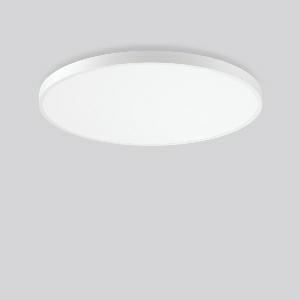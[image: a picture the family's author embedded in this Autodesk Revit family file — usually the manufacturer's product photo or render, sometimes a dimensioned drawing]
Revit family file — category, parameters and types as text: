
# Revit family: triona_round_a_312391_002_2_76_6565
name_source: partatom
category: Lighting Fixtures
units: mm (PartAtom-declared; Revit-internal decimal feet)

## family parameters
Cut with Voids When Loaded = No
Host = Face
Light Source = No
Part Type = Normal
Room Calculation Point = No
Round Connector Dimension = Use Diameter
Shared = No

## types (1)
- TuneableWhite 846 (1 x LED Modul 846, 5700 lm, 4600)
    Apparent Load = 61 VA
    CIE Flux Codes = 50 80 96 100 100
    Color Rendering = 80
    Color Temperature = 4600
    Default Elevation = 1800 mm
    Description = Series: TRIONA round
Decorative round LED surface-mounted luminaire. Flat, seamless frame: aluminium extrusion profile, powder coated. Cover made of sheet steel, powder-coated. Light emission through a diffuser: plastic, opal. Lightguide and diffuser made of non-yellowing plastic (PMMA). Lateral light emission (RZB SIDELITE technology) for above-average homogeneous light distribution. Tunable white versions, dynamically adjustable from 2700 K to 6500 K. Suitable for Ceiling mounting, Wall (surface). Tool-free mounting via bayonet connection. Electronic ballast included. Very easy installation thanks to Plug+Play connection. Ideal for use as part of the Human Centric Lighting concept in connection with RZB light management systems. 
Colour: traffic white, matt (RAL 9016)
Diameter: 1009 mm
Height: 88 mm
Lamp: LED
Socket: without socket
Colour temperature: 2700K - 6500K
Colour rendering index (CRI): 80
System power: 61 W
Rated luminous flux: 5700 lm
Luminous efficiency: 93 lm/W
System power 2: 63 W
Rated luminous flux 2: 5450 lm
Luminous efficiency 2: 87 lm/W
System power 3: 63 W
Rated luminous flux 3: 5500 lm
Luminous efficiency 3: 87 lm/W
Control gear: Converter, dimmable, DALI
Protection class: I
Type of protection: IP 20
    Height = 88 mm
    Lamp = 1 x LED Modul 846
    Lamp Light Flux = 5700 lm
    Lamp count = 1
    Length = 1009 mm
    Lifetime = 50000 h
    Luminous efficacy = 93 lm/W
    Manufacturer = RZB
    ModVariant = No
    Model = 312391.002.2.76
    Mounting Place = Ceiling
    Mounting Type = Surface mounted
    Number of Poles = 1
    OnlyDefault = Yes
    Power Factor = 1
    Product Name = TRIONA round A
    Product group = Surface mounted modular luminaires
    ProductGroupID = 306
    Protection Class = Protection class I
    Protection Degree = IP 20
    RLX_Detail_Level = 1
    RLX_Emergency_Light_Flux = 0 lm
    RLX_Emergency_Type = 0
    RLX_Emergency_Type_DB = No
    RlxData = <blob elided: 36333 chars, md5=0d89ba1d>
    Socket = socket
    Standby Power = 0 W
    System Light Flux = 5700 lm
    System Power = 61 W
    Type Comments = TuneableWhite 846
    Type Image = 312392.002.jpg
    URL = http://relux.com
    VarID = tuneablewhite_846
    Voltage = 230 V
    Voltage Range = 220-240 V
    Weight = 0.00 kg
    Width = 0 mm  [stored 0 ft]

note: [stored X ft] marks values corroborated as IEEE doubles in the binary element streams (Revit-internal decimal feet)

## geometry (parser evidence)
native form markers: Blend x4, Sweep x8
no freeform markers — native parametric forms only
